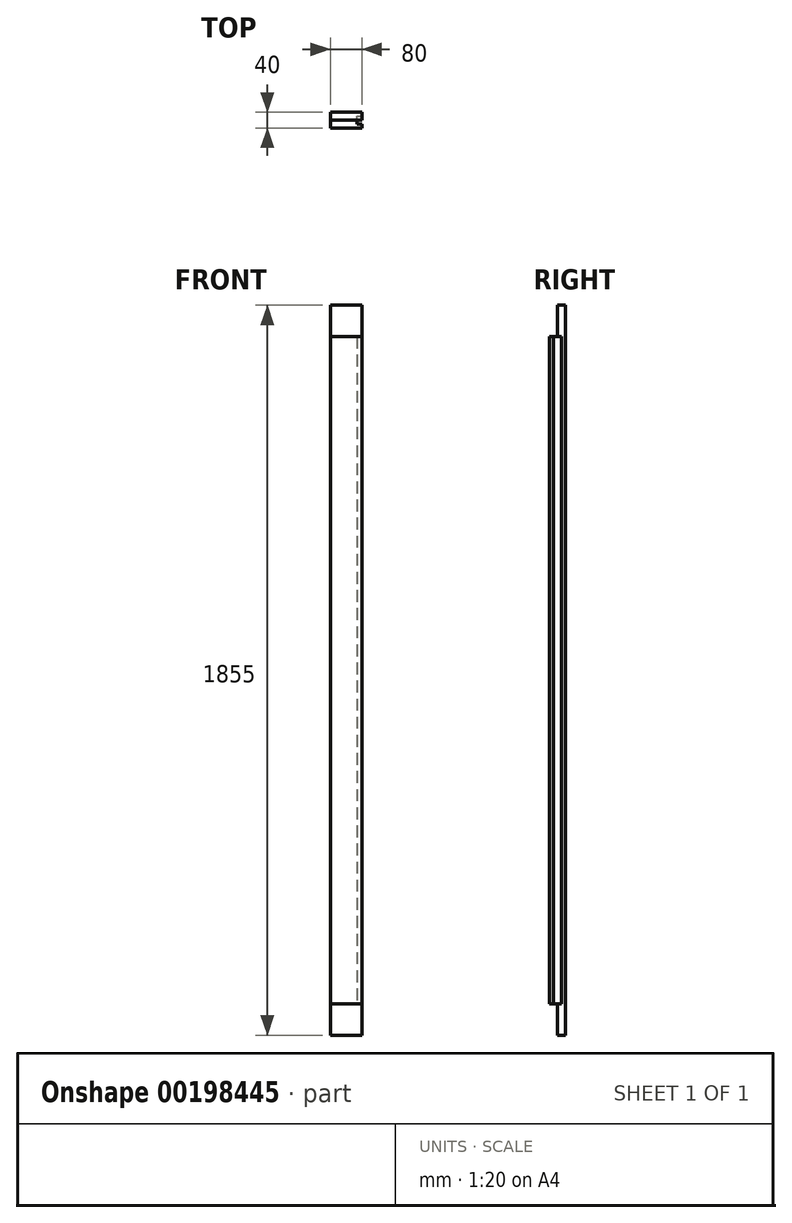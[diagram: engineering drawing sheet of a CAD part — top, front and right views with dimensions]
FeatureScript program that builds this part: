
annotation { "Feature Type Name" : "Feature", "Feature Type Description" : "" }
export const myFeature = defineFeature(function(context is Context, id is Id, definition is map)
    precondition{}
    {
        {
            var Q0;
            Q0=qCreatedBy(makeId("Right.planeOp"),FACE);
            var sketch = newSketch(context, id + "F0", { "sketchPlane" : qUnion([Q0])});
            skLineSegment(sketch, "E0.bottom", {"start": v(20, 6.63) * mm, "end": v(40, 6.63) * mm});
            skLineSegment(sketch, "E0.top", {"start": v(20, 1861.63) * mm, "end": v(40, 1861.63) * mm});
            skLineSegment(sketch, "E0.left", {"start": v(0, 86.63) * mm, "end": v(0, 1781.63) * mm});
            skLineSegment(sketch, "E0.right", {"start": v(40, 6.63) * mm, "end": v(40, 1861.63) * mm});
            skLineSegment(sketch, "E1.top", {"start": v(0, 86.63) * mm, "end": v(20, 86.63) * mm});
            skLineSegment(sketch, "E1.right", {"start": v(20, 6.63) * mm, "end": v(20, 86.63) * mm});
            skLineSegment(sketch, "E2.top", {"start": v(0, 1781.63) * mm, "end": v(20, 1781.63) * mm});
            skLineSegment(sketch, "E2.right", {"start": v(20, 1861.63) * mm, "end": v(20, 1781.63) * mm});
            skSolve(sketch);
        }
        {
            var Q0;
            Q0=makeQuery(id+"F0.imprint","IMPRINT",FACE,{"disambiguationData":[TD([[makeQuery(id+"F0.imprint","IMPRINT",EDGE,{"derivedFrom":sQuery(id+"F0.wireOp",EDGE,"E0.bottom")}),1.0]])]});
            extrude(context, id + "F1", {"entities" : qUnion([Q0]), "depth" : 80 * mm});
        }
        {
            var Q0;
            Q0=makeQuery(id+"F1.opExtrude","CAP_FACE",FACE,{"disambiguationData":[OSD([sQuery(id+"F0.wireOp",EDGE,"E0.bottom"),sQuery(id+"F0.wireOp",EDGE,"E0.top"),sQuery(id+"F0.wireOp",EDGE,"E0.left"),sQuery(id+"F0.wireOp",EDGE,"E0.right"),sQuery(id+"F0.wireOp",EDGE,"E1.top"),sQuery(id+"F0.wireOp",EDGE,"E1.right"),sQuery(id+"F0.wireOp",EDGE,"E2.top"),sQuery(id+"F0.wireOp",EDGE,"E2.right")])],"isStart":false});
            var sketch = newSketch(context, id + "F2", { "sketchPlane" : qUnion([Q0])});
            skLineSegment(sketch, "E3.bottom", {"start": v(10, 1781.63) * mm, "end": v(30, 1781.63) * mm});
            skLineSegment(sketch, "E3.top", {"start": v(10, 86.63) * mm, "end": v(30, 86.63) * mm});
            skLineSegment(sketch, "E3.left", {"start": v(10, 1781.63) * mm, "end": v(10, 86.63) * mm});
            skLineSegment(sketch, "E3.right", {"start": v(30, 1781.63) * mm, "end": v(30, 86.63) * mm});
            skSolve(sketch);
        }
        {
            var Q0;
            {var subQ2=sQuery(id+"F2.wireOp",EDGE,"E3.left");Q0=makeQuery(id+"F2.imprint","IMPRINT",FACE,{"disambiguationData":[TD([[makeQuery(id+"F2.imprint","IMPRINT",EDGE,{"derivedFrom":subQ2}),1.0]])]});}
            extrude(context, id + "F3", {"entities" : qUnion([Q0]), "operationType" : NewBodyOperationType.REMOVE, "oppositeDirection" : true, "depth" : 12 * mm});
        }
    });
